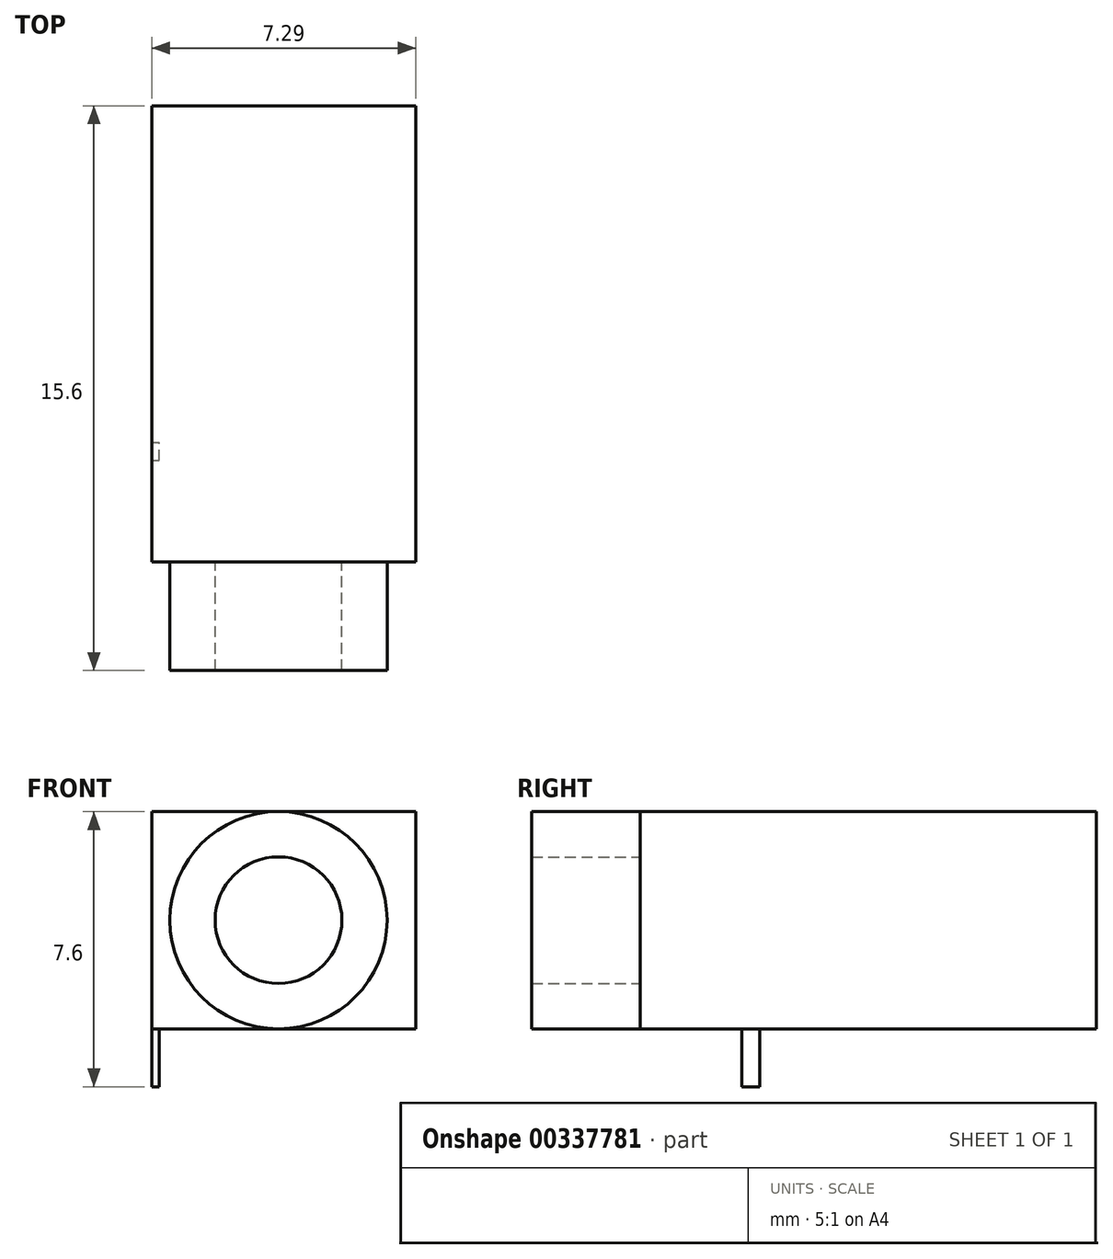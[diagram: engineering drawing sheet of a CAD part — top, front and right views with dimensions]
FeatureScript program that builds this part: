
annotation { "Feature Type Name" : "Feature", "Feature Type Description" : "" }
export const myFeature = defineFeature(function(context is Context, id is Id, definition is map)
    precondition{}
    {
        {
            var Q0;
            Q0=qCreatedBy(makeId("Top.planeOp"),FACE);
            var sketch = newSketch(context, id + "F0", { "sketchPlane" : qUnion([Q0])});
            skLineSegment(sketch, "E0.bottom", {"start": v(-3.5, -3.4) * mm, "end": v(3.8, -3.4) * mm});
            skLineSegment(sketch, "E0.top", {"start": v(-3.5, 9.2) * mm, "end": v(3.8, 9.2) * mm});
            skLineSegment(sketch, "E0.left", {"start": v(-3.5, -3.4) * mm, "end": v(-3.5, 9.2) * mm});
            skLineSegment(sketch, "E0.right", {"start": v(3.8, -3.4) * mm, "end": v(3.8, 9.2) * mm});
            skSolve(sketch);
        }
        {
            var Q0;
            Q0=makeQuery(id+"F0.imprint","IMPRINT",FACE,{"disambiguationData":[TD([[makeQuery(id+"F0.imprint","IMPRINT",EDGE,{"derivedFrom":sQuery(id+"F0.wireOp",EDGE,"E0.bottom")}),1.0]])]});
            extrude(context, id + "F1", {"entities" : qUnion([Q0]), "depth" : 6 * mm});
        }
        {
            var Q0;
            Q0=makeQuery(id+"F1.opExtrude","SWEPT_FACE",FACE,{"disambiguationData":[OSD([sQuery(id+"F0.wireOp",EDGE,"E0.bottom")])]});
            var sketch = newSketch(context, id + "F2", { "sketchPlane" : qUnion([Q0])});
            skCircle(sketch, "E1", {"center": v(0, 0) * mm, "radius": 3 * mm, "construction": true});
            skCircle(sketch, "E2", {"center": v(0, 3) * mm, "radius": 3 * mm});
            skCircle(sketch, "E3", {"center": v(0, 3) * mm, "radius": 1.75 * mm});
            skSolve(sketch);
        }
        {
            var Q0;
            Q0 = qSketchRegion(id + "F2", true);
            extrude(context, id + "F3", {"entities" : qUnion([Q0]), "operationType" : NewBodyOperationType.ADD, "depth" : 3 * mm});
        }
        {
            var Q0;
            Q0=makeQuery(id+"F1.opExtrude","CAP_FACE",FACE,{"disambiguationData":[OSD([sQuery(id+"F0.wireOp",EDGE,"E0.bottom"),sQuery(id+"F0.wireOp",EDGE,"E0.top"),sQuery(id+"F0.wireOp",EDGE,"E0.left"),sQuery(id+"F0.wireOp",EDGE,"E0.right")])],"isStart":true});
            var sketch = newSketch(context, id + "F4", { "sketchPlane" : qUnion([Q0])});
            skLineSegment(sketch, "E4.bottom", {"start": v(-3.5, 0.6) * mm, "end": v(-3.3, 0.6) * mm});
            skLineSegment(sketch, "E4.top", {"start": v(-3.5, 0.1) * mm, "end": v(-3.3, 0.1) * mm});
            skLineSegment(sketch, "E4.left", {"start": v(-3.5, 0.6) * mm, "end": v(-3.5, 0.1) * mm});
            skLineSegment(sketch, "E4.right", {"start": v(-3.3, 0.6) * mm, "end": v(-3.3, 0.1) * mm});
            skSolve(sketch);
        }
        {
            var Q0;
            Q0 = qSketchRegion(id + "F4", true);
            extrude(context, id + "F5", {"entities" : qUnion([Q0]), "operationType" : NewBodyOperationType.ADD, "depth" : 1.6 * mm});
        }
    });
